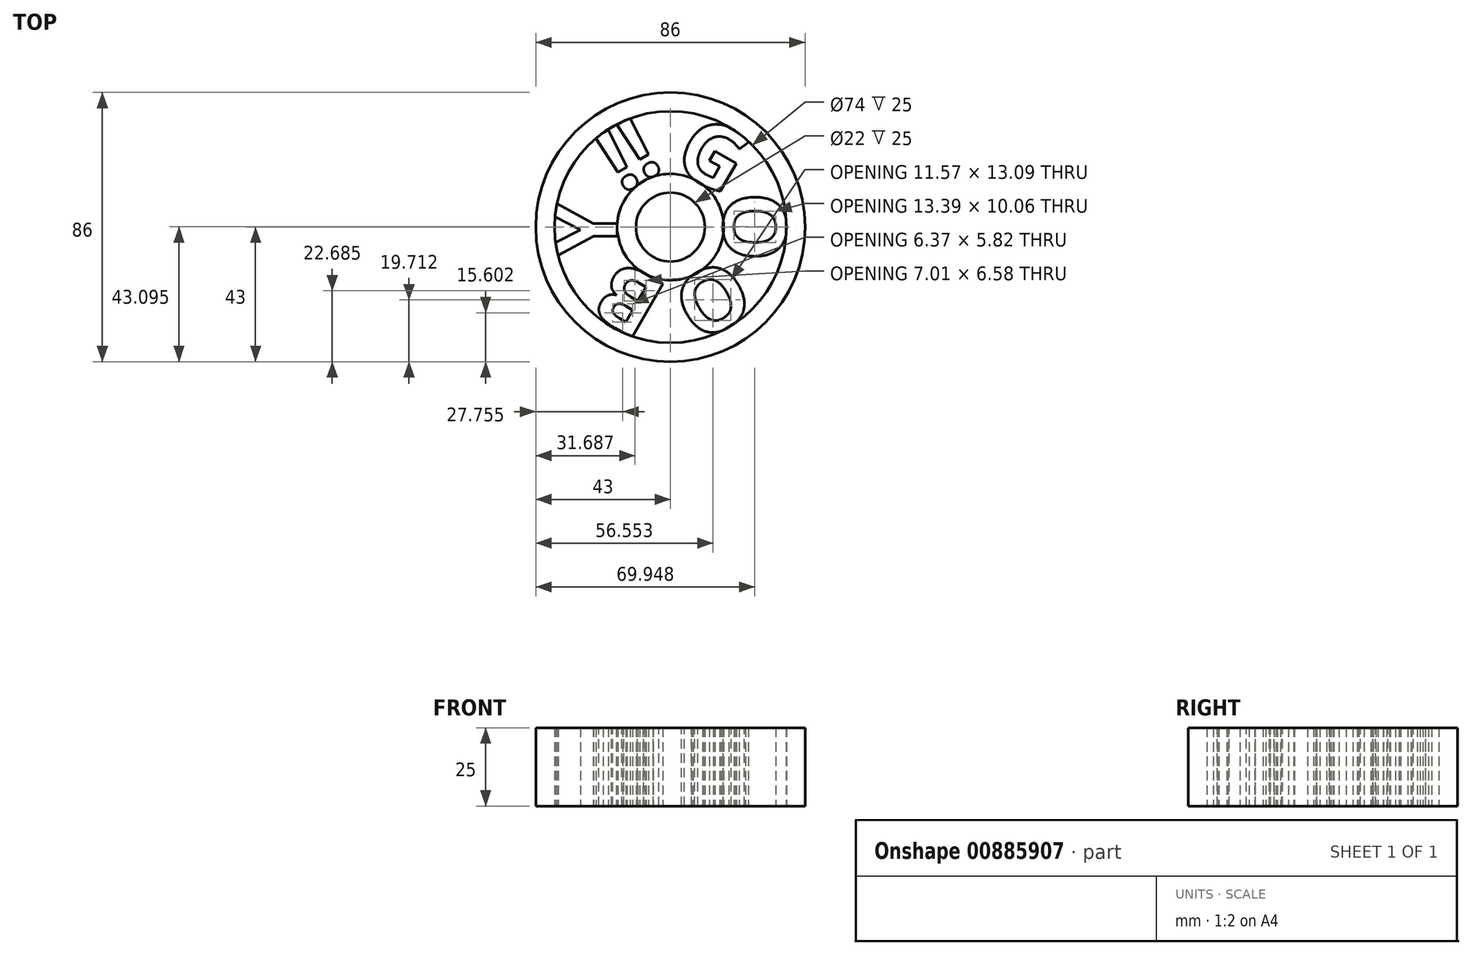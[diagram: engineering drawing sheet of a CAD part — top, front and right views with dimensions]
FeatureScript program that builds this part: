
annotation { "Feature Type Name" : "Feature", "Feature Type Description" : "" }
export const myFeature = defineFeature(function(context is Context, id is Id, definition is map)
    precondition{}
    {
        {
            var Q0;
            Q0=qCreatedBy(makeId("Top.planeOp"),FACE);
            var sketch = newSketch(context, id + "F0", { "sketchPlane" : qUnion([Q0])});
            skCircle(sketch, "E0", {"center": v(0, 0) * mm, "radius": 17 * mm});
            skCircle(sketch, "E1", {"center": v(0, 0) * mm, "radius": 11 * mm});
            skText(sketch, "E2", { "text": "G", "fontName": "OpenSans-Bold.ttf"});
            skText(sketch, "E3", { "text": "O", "fontName": "OpenSans-Bold.ttf"});
            skText(sketch, "E4", { "text": "O", "fontName": "OpenSans-Bold.ttf"});
            skText(sketch, "E5", { "text": "B", "fontName": "OpenSans-Bold.ttf"});
            skLineSegment(sketch, "E6", {"start": v(0, 37) * mm, "end": v(0, -37) * mm, "construction": true});
            skLineSegment(sketch, "E7", {"start": v(32.04, 18.5) * mm, "end": v(-32.04, -18.5) * mm, "construction": true});
            skLineSegment(sketch, "E8", {"start": v(-32.04, 18.5) * mm, "end": v(32.04, -18.5) * mm, "construction": true});
            skPoint(sketch, "E9", {"position": v(0, 17) * mm});
            skPoint(sketch, "E10", {"position": v(14.72, 8.5) * mm});
            skPoint(sketch, "E11", {"position": v(14.72, -8.5) * mm});
            skPoint(sketch, "E12", {"position": v(0, -17) * mm});
            skPoint(sketch, "E13", {"position": v(-14.72, -8.5) * mm});
            skPoint(sketch, "E14", {"position": v(-14.72, 8.5) * mm});
            skText(sketch, "E15", { "text": "Y", "fontName": "OpenSans-Bold.ttf"});
            skLineSegment(sketch, "E16", {"start": v(43, 0) * mm, "end": v(-37, 0) * mm, "construction": true});
            skLineSegment(sketch, "E17", {"start": v(-21, 36.37) * mm, "end": v(21.5, -37.24) * mm, "construction": true});
            skLineSegment(sketch, "E18", {"start": v(18.5, 32.04) * mm, "end": v(-18.5, -32.04) * mm, "construction": true});
            skPoint(sketch, "E19", {"position": v(-8.5, 14.72) * mm});
            skCircle(sketch, "E20", {"center": v(0, 0) * mm, "radius": 37 * mm});
            skCircle(sketch, "E21.0", {"center": v(0, 0) * mm, "radius": 43 * mm});
            skPoint(sketch, "E22.orphan", {"position": v(82.26, 0) * mm});
            skPoint(sketch, "E23.orphan", {"position": v(0, 69.3) * mm});
            skPoint(sketch, "E24", {"position": v(0, 43) * mm});
            skPoint(sketch, "E25", {"position": v(0, -43) * mm});
            skText(sketch, "E26", { "text": "!!", "fontName": "OpenSans-Bold.ttf"});
            const initialGuessF0  = {"E2": [-3e-05, 0.01965, 0.86603, -0.5, 0.02], "E3": [0.017, 0.01115, 0, -1, 0.02], "E4": [0.01815, -0.00915, -0.86603, -0.5, 0.02], "E5": [-0.00027, -0.01947, -0.86603, 0.5, 0.02], "E15": [-0.017, -0.00957, 0, 1, 0.02], "E26": [-0.01546, 0.0107, 0.86603, 0.5, 0.02]};
            skSetInitialGuess(sketch, initialGuessF0);
            skSolve(sketch);
        }
        {
            var Q0;
            {var subQ6=sQuery(id+"F0.wireOp",EDGE,"E15.sketch_text.stroke-0");Q0=makeQuery(id+"F0.imprint","IMPRINT",FACE,{"disambiguationData":[TD([[makeQuery(id+"F0.imprint","IMPRINT",EDGE,{"derivedFrom":subQ6}),-1.0]])]});}
            var Q1;
            {var subQ7=sQuery(id+"F0.wireOp",EDGE,"E5.sketch_text.stroke-1");Q1=makeQuery(id+"F0.imprint","IMPRINT",FACE,{"disambiguationData":[TD([[makeQuery(id+"F0.imprint","IMPRINT",EDGE,{"derivedFrom":subQ7}),-1.0]])]});}
            var Q2;
            {var subQ13=sQuery(id+"F0.wireOp",EDGE,"E4.sketch_text.stroke-0");Q2=makeQuery(id+"F0.imprint","IMPRINT",FACE,{"disambiguationData":[TD([[makeQuery(id+"F0.imprint","IMPRINT",EDGE,{"derivedFrom":subQ13}),-1.0]])]});}
            var Q3;
            {var subQ13=sQuery(id+"F0.wireOp",EDGE,"E3.sketch_text.stroke-0");Q3=makeQuery(id+"F0.imprint","IMPRINT",FACE,{"disambiguationData":[TD([[makeQuery(id+"F0.imprint","IMPRINT",EDGE,{"derivedFrom":subQ13}),-1.0]])]});}
            var Q4;
            Q4=makeQuery(id+"F0.imprint","IMPRINT",FACE,{"disambiguationData":[TD([[makeQuery(id+"F0.imprint","IMPRINT",EDGE,{"derivedFrom":sQuery(id+"F0.wireOp",EDGE,"E2.sketch_text.stroke-0")}),-1.0]])]});
            var Q5;
            Q5=makeQuery(id+"F0.imprint","IMPRINT",FACE,{"disambiguationData":[TD([[makeQuery(id+"F0.imprint","IMPRINT",EDGE,{"derivedFrom":sQuery(id+"F0.wireOp",EDGE,"E26.sketch_text.stroke-16")}),-1.0]])]});
            var Q6;
            Q6=makeQuery(id+"F0.imprint","IMPRINT",FACE,{"disambiguationData":[TD([[makeQuery(id+"F0.imprint","IMPRINT",EDGE,{"derivedFrom":sQuery(id+"F0.wireOp",EDGE,"E26.sketch_text.stroke-4")}),-1.0]])]});
            var Q7;
            {var subQ5=sQuery(id+"F0.wireOp",EDGE,"E26.sketch_text.stroke-0");Q7=makeQuery(id+"F0.imprint","IMPRINT",FACE,{"disambiguationData":[TD([[makeQuery(id+"F0.imprint","IMPRINT",EDGE,{"derivedFrom":subQ5}),-1.0]])]});}
            var Q8;
            {var subQ1=sQuery(id+"F0.wireOp",EDGE,"E26.sketch_text.stroke-12");Q8=makeQuery(id+"F0.imprint","IMPRINT",FACE,{"disambiguationData":[TD([[makeQuery(id+"F0.imprint","IMPRINT",EDGE,{"derivedFrom":subQ1}),-1.0]])]});}
            extrude(context, id + "F1", {"entities" : qUnion([Q0, Q1, Q2, Q3, Q4, Q5, Q6, Q7, Q8]), "depth" : 25 * mm, "offsetDistance" : 25 * mm});
        }
        {
            var Q0;
            Q0 = qSketchRegion(id + "F0", true);
            var Q1;
            {var subQ0=sQuery(id+"F0.wireOp",EDGE,"E26.sketch_text.stroke-2");var subQ1=sQuery(id+"F0.wireOp",EDGE,"E20");var subQ2=makeQuery(id+"F0.imprint","INTERSECT",VERTEX,{"derivedFrom":[subQ1,subQ0]});Q1=makeQuery(id+"F0.imprint","IMPRINT",FACE,{"disambiguationData":[TD([[makeQuery(id+"F0.imprint","IMPRINT",EDGE,{"disambiguationData":[TD([[subQ2,-1.0]])],"derivedFrom":subQ1}),-1.0]])]});}
            var Q2;
            {var subQ0=sQuery(id+"F0.wireOp",EDGE,"E26.sketch_text.stroke-15");var subQ1=sQuery(id+"F0.wireOp",EDGE,"E20");var subQ2=makeQuery(id+"F0.imprint","INTERSECT",VERTEX,{"derivedFrom":[subQ1,subQ0]});Q2=makeQuery(id+"F0.imprint","IMPRINT",FACE,{"disambiguationData":[TD([[makeQuery(id+"F0.imprint","IMPRINT",EDGE,{"disambiguationData":[TD([[subQ2,-1.0]])],"derivedFrom":subQ1}),-1.0]])]});}
            var Q3;
            {var subQ0=sQuery(id+"F0.wireOp",EDGE,"E2.sketch_text.stroke-8");var subQ1=sQuery(id+"F0.wireOp",EDGE,"E2.sketch_text.stroke-7");var subQ2=makeQuery(id+"F0.imprint","INTERSECT",VERTEX,{"derivedFrom":[subQ1,subQ0]});Q3=makeQuery(id+"F0.imprint","IMPRINT",FACE,{"disambiguationData":[TD([[makeQuery(id+"F0.imprint","IMPRINT",EDGE,{"disambiguationData":[TD([[subQ2,1.0]])],"derivedFrom":subQ1}),-1.0]])]});}
            var Q4;
            {var subQ0=sQuery(id+"F0.wireOp",EDGE,"E3.sketch_text.stroke-6");var subQ1=sQuery(id+"F0.wireOp",EDGE,"E3.sketch_text.stroke-5");var subQ2=makeQuery(id+"F0.imprint","INTERSECT",VERTEX,{"derivedFrom":[subQ1,subQ0]});Q4=makeQuery(id+"F0.imprint","IMPRINT",FACE,{"disambiguationData":[TD([[makeQuery(id+"F0.imprint","IMPRINT",EDGE,{"disambiguationData":[TD([[subQ2,1.0]])],"derivedFrom":subQ1}),-1.0]])]});}
            var Q5;
            {var subQ0=sQuery(id+"F0.wireOp",EDGE,"E5.sketch_text.stroke-11");var subQ1=sQuery(id+"F0.wireOp",EDGE,"E5.sketch_text.stroke-0");var subQ2=makeQuery(id+"F0.imprint","INTERSECT",VERTEX,{"derivedFrom":[subQ1,subQ0]});Q5=makeQuery(id+"F0.imprint","IMPRINT",FACE,{"disambiguationData":[TD([[makeQuery(id+"F0.imprint","IMPRINT",EDGE,{"disambiguationData":[TD([[subQ2,-1.0]])],"derivedFrom":subQ1}),-1.0]])]});}
            var Q6;
            {var subQ0=sQuery(id+"F0.wireOp",EDGE,"E4.sketch_text.stroke-6");var subQ1=sQuery(id+"F0.wireOp",EDGE,"E4.sketch_text.stroke-5");var subQ2=makeQuery(id+"F0.imprint","INTERSECT",VERTEX,{"derivedFrom":[subQ1,subQ0]});Q6=makeQuery(id+"F0.imprint","IMPRINT",FACE,{"disambiguationData":[TD([[makeQuery(id+"F0.imprint","IMPRINT",EDGE,{"disambiguationData":[TD([[subQ2,1.0]])],"derivedFrom":subQ1}),-1.0]])]});}
            var Q7;
            {var subQ0=sQuery(id+"F0.wireOp",EDGE,"E15.sketch_text.stroke-7");Q7=makeQuery(id+"F0.imprint","IMPRINT",FACE,{"disambiguationData":[TD([[makeQuery(id+"F0.imprint","IMPRINT",EDGE,{"derivedFrom":subQ0}),-1.0]])]});}
            var Q8;
            {var subQ0=sQuery(id+"F0.wireOp",EDGE,"E15.sketch_text.stroke-2");var subQ1=sQuery(id+"F0.wireOp",EDGE,"E15.sketch_text.stroke-1");var subQ2=makeQuery(id+"F0.imprint","INTERSECT",VERTEX,{"derivedFrom":[subQ1,subQ0]});Q8=makeQuery(id+"F0.imprint","IMPRINT",FACE,{"disambiguationData":[TD([[makeQuery(id+"F0.imprint","IMPRINT",EDGE,{"disambiguationData":[TD([[subQ2,1.0]])],"derivedFrom":subQ1}),-1.0]])]});}
            extrude(context, id + "F2", {"entities" : qUnion([Q0, Q1, Q2, Q3, Q4, Q5, Q6, Q7, Q8]), "depth" : 25 * mm, "offsetDistance" : 25 * mm});
        }
        {
            var Q0;
            Q0=makeQuery(id+"F0.imprint","IMPRINT",FACE,{"disambiguationData":[TD([[makeQuery(id+"F0.imprint","IMPRINT",EDGE,{"derivedFrom":sQuery(id+"F0.wireOp",EDGE,"E1")}),-1.0]])]});
            extrude(context, id + "F3", {"entities" : qUnion([Q0]), "depth" : 25 * mm, "offsetDistance" : 25 * mm});
        }
    });
